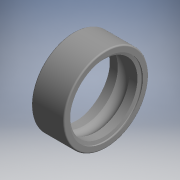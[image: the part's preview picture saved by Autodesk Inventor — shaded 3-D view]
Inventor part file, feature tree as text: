
AUTODESK INVENTOR PART (.ipt)
format: ipt  version: 2017.3 (Build 213256000, 256)  size: 158,720 bytes
history: native  units: mm (DEFAULTED — no unit token found)
features: revolve x1, sketch x1
ambient origin geometry x8: Origin, YZ Plane, XZ Plane, XY Plane, X Axis, Y Axis, Z Axis, Center Point
bodies: Solid1 (feature_tree)
feature tree (2):
  revolve  "Revolution1"  [1 undecoded]
  sketch  "Sketch_22"  dims[d0=360.0deg]
note: 1 required parameter value undecoded (feature->parameter linkage not recoverable at this tier; creation-order binding heuristic only, values carry confidence <= 0.55)
